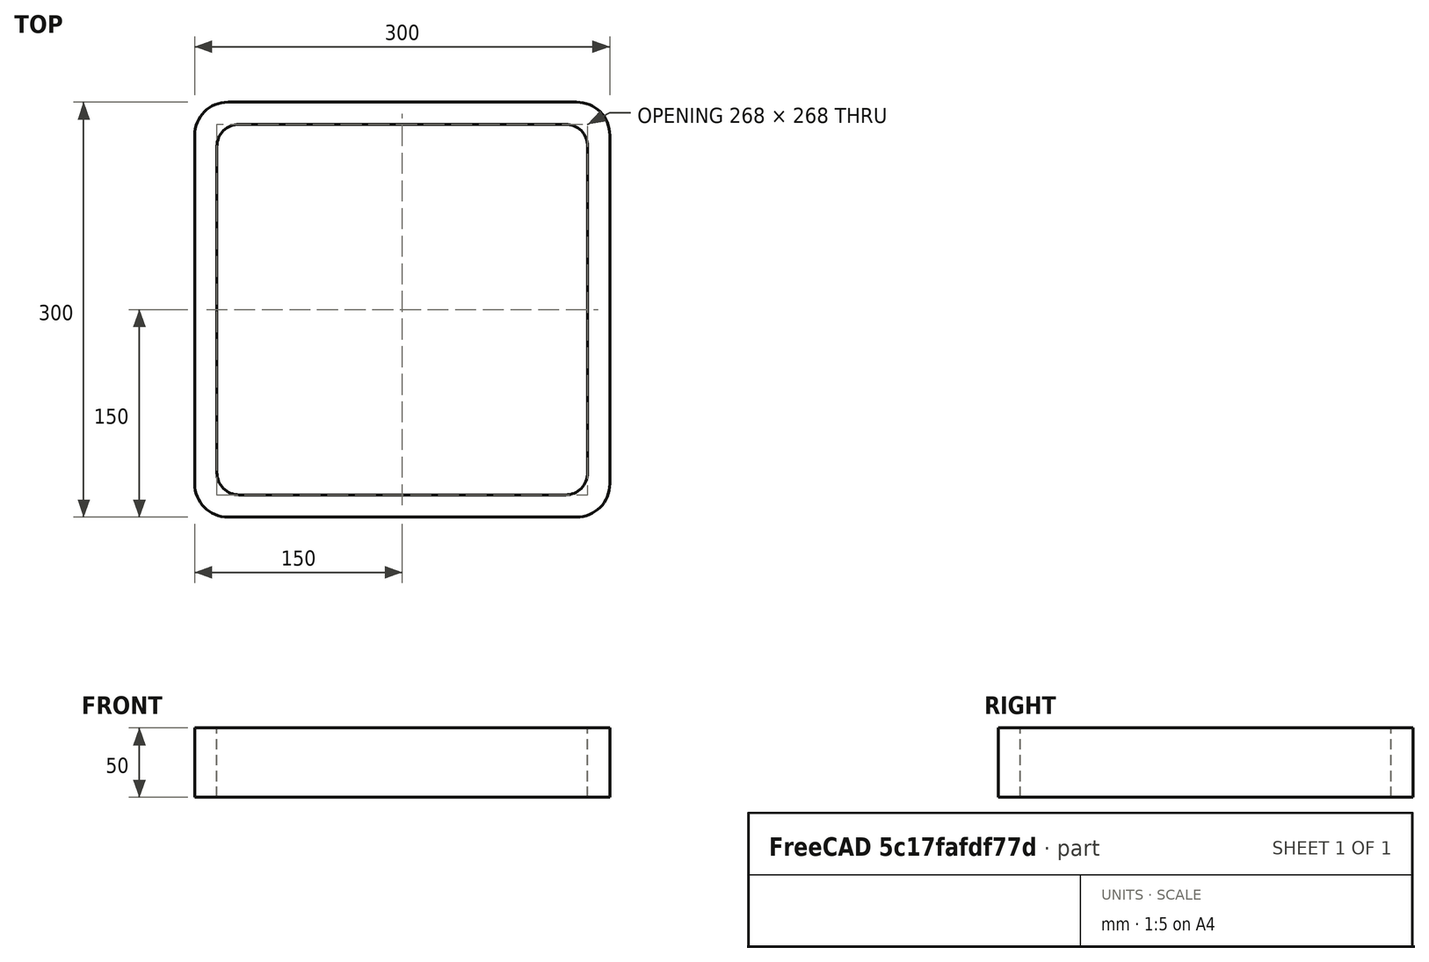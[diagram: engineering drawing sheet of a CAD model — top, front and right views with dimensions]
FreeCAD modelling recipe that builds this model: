
FCSTD DOCUMENT  (FreeCAD 0.15R4671 (Git))
Label: Square hollow section 300x300x16 EN10219 S235JRH
License: All rights reserved
LicenseURL: http://en.wikipedia.org/wiki/All_rights_reserved
objects: Sketcher::SketchObject×1, Part::Extrusion×1
note: 2 computed .brp shape members not serialized (recipe doc carries the construction recipe); baked Part::Feature solids carry a one-line shape summary decoded from their .brp

FEATURE [Sketcher::SketchObject] Sketch
  sketch-geometry (16):
    g0: LineSegment StartX=-118 StartY=134 StartZ=0 EndX=118 EndY=134 EndZ=0
    g1: LineSegment StartX=134 StartY=118 StartZ=0 EndX=134 EndY=-118 EndZ=0
    g2: LineSegment StartX=118 StartY=-134 StartZ=0 EndX=-118 EndY=-134 EndZ=0
    g3: LineSegment StartX=-134 StartY=-118 StartZ=0 EndX=-134 EndY=118 EndZ=0
    g4: LineSegment StartX=-126 StartY=150 StartZ=0 EndX=126 EndY=150 EndZ=0
    g5: LineSegment StartX=150 StartY=126 StartZ=0 EndX=150 EndY=-126 EndZ=0
    g6: LineSegment StartX=126 StartY=-150 StartZ=0 EndX=-126 EndY=-150 EndZ=0
    g7: LineSegment StartX=-150 StartY=-126 StartZ=0 EndX=-150 EndY=126 EndZ=0
    g8: ArcOfCircle CenterX=-118 CenterY=118 CenterZ=0 NormalX=0 NormalY=0 NormalZ=1 Radius=16 StartAngle=1.5708 EndAngle=3.14159
    g9: ArcOfCircle CenterX=118 CenterY=118 CenterZ=0 NormalX=0 NormalY=0 NormalZ=1 Radius=16 StartAngle=0 EndAngle=1.5708
    g10: ArcOfCircle CenterX=118 CenterY=-118 CenterZ=0 NormalX=0 NormalY=0 NormalZ=1 Radius=16 StartAngle=4.71239 EndAngle=6.28319
    g11: ArcOfCircle CenterX=-118 CenterY=-118 CenterZ=0 NormalX=0 NormalY=0 NormalZ=1 Radius=16 StartAngle=3.14159 EndAngle=4.71239
    g12: ArcOfCircle CenterX=126 CenterY=126 CenterZ=0 NormalX=0 NormalY=0 NormalZ=1 Radius=24 StartAngle=0 EndAngle=1.5708
    g13: ArcOfCircle CenterX=126 CenterY=-126 CenterZ=0 NormalX=0 NormalY=0 NormalZ=1 Radius=24 StartAngle=4.71239 EndAngle=6.28319
    g14: ArcOfCircle CenterX=-126 CenterY=-126 CenterZ=0 NormalX=0 NormalY=0 NormalZ=1 Radius=24 StartAngle=3.14159 EndAngle=4.71239
    g15: ArcOfCircle CenterX=-126 CenterY=126 CenterZ=0 NormalX=0 NormalY=0 NormalZ=1 Radius=24 StartAngle=1.5708 EndAngle=3.14159
  constraints (36):
    c: Horizontal(g2)
    c: Vertical(g3)
    c: Horizontal(g6)
    c: Vertical(g7)
    c: Tangent(g3,g8) = 1.5708
    c: Tangent(g0,g8) = 1.5708
    c: Tangent(g0,g9) = 1.5708
    c: Tangent(g1,g9) = 1.5708
    c: Tangent(g1,g10) = 1.5708
    c: Tangent(g2,g10) = 1.5708
    c: Tangent(g2,g11) = 1.5708
    c: Tangent(g3,g11) = 1.5708
    c: Tangent(g4,g12) = 1.5708
    c: Tangent(g5,g12) = 1.5708
    c: Tangent(g5,g13) = 1.5708
    c: Tangent(g6,g13) = 1.5708
    c: Tangent(g6,g14) = 1.5708
    c: Tangent(g7,g14) = 1.5708
    c: Tangent(g7,g15) = 1.5708
    c: Tangent(g4,g15) = 1.5708
    c: Equal(g9,g8)
    c: Equal(g9,g11)
    c: Equal(g9,g10)
    c: Equal(g12,g15)
    c: Equal(g12,g14)
    c: Equal(g12,g13)
    c: Symmetric(g4,g6,g-1)
    c: Symmetric(g7,g5,g-2)
    c: DistanceY(g4,g6) = -300
    c: DistanceX(g7,g5) = 300
    c: Symmetric(g3,g1,g-2)
    c: Symmetric(g0,g2,g-1)
    c: DistanceY(g0,g4) = 16
    c: DistanceX(g5,g1) = -16
    c: Radius(g9) = 16
    c: Radius(g12) = 24
FEATURE [Part::Extrusion] Extrude  label="Square hollow section 300x300x16 EN10219 S235JRH"
  Base = -> Sketch
  Dir = (0,0,50)
  Solid = true
